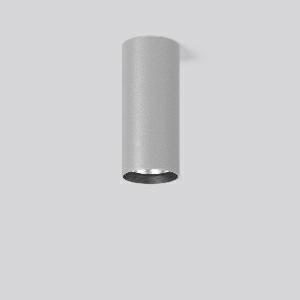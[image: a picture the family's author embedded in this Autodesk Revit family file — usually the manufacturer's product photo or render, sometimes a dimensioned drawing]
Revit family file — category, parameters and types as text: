
# Revit family: heledon_mini_a_931202_004_1_76_789c
name_source: partatom
category: Lighting Fixtures
units: mm (PartAtom-declared; Revit-internal decimal feet)

## family parameters
Cut with Voids When Loaded = No
Host = Face
Light Source = No
Part Type = Normal
Room Calculation Point = No
Round Connector Dimension = Use Diameter
Shared = No

## types (1)
- HELEDON mini A (1 x LED Modul 940, 2750 lm, 4000)
    Apparent Load = 20 VA
    Approval mark = CE
    CIE Flux Codes = 95 99 100 100 100
    Color Rendering = 92
    Color Temperature = 4000
    Default Elevation = 1800 mm
    Description = Series: HELEDON mini
Cylindrical surface-mounted downlight. Housing: die-cast aluminium, powder-coated. Internal ceiling frame polycarbonate with bayonet mounting. Black plastic ring and recessed LED to prevent glare from the side. Optical assembly with reflector made of MIRO-Silver with 98% total light reflection for outstanding efficiency - can be changed without tools. Best colour rendering index Ra>90. Suitable for Ceiling mounting. Easy installation with a separate ceiling frame with bayonet mounting and plug connection. Driver integrated. Connected via plug-in connector. High quality converter without flickering and stroboscopic effect. The following accessories can be mounted without use of tools: interchangeable lenses, decorative glasses, honeycomb louvre, clear and frosted diffusers, white interchangeable plastic ring. 
Colour: silver
Diameter: 87 mm
Height: 197 mm
Lamp: LED
Socket: without socket
Colour temperature: 4000K
Colour rendering index (CRI): 92
System power: 20 W
Rated luminous flux: 2750 lm
Luminous efficiency: 138 lm/W
Control gear: Converter, dimmable, DALI
Protection class: I
Type of protection: IP 20
    Height = 197 mm
    Lamp = 1 x LED Modul 940
    Lamp Light Flux = 2750 lm
    Lamp count = 1
    Length = 87 mm
    Lifetime = 50000 h
    Luminous efficacy = 138 lm/W
    Manufacturer = RZB
    ModVariant = No
    Model = 931202.004.1.76
    Mounting Place = Ceiling
    Mounting Type = Surface mounted
    Number of Poles = 1
    OnlyDefault = Yes
    Power Factor = 1
    Product Name = HELEDON mini A
    Product group = Surface mounted downlights
    ProductGroupID = 302
    Protection Class = Protection class I
    Protection Degree = IP 20
    RLX_Detail_Level = 1
    RLX_Emergency_Light_Flux = 0 lm
    RLX_Emergency_Type = 0
    RLX_Emergency_Type_DB = No
    RlxData = <blob elided: 107537 chars, md5=f5f3c9b7>
    Socket = socket
    Standby Power = 0 W
    System Light Flux = 2750 lm
    System Power = 20 W
    Type Comments = Product without accessories
    Type Image = 931188.004.jpg
    URL = http://relux.com
    VarID = ---
    Voltage = 230 V
    Voltage Range = 220-240 V
    Weight = 0.00 kg
    Width = 0 mm  [stored 0 ft]

note: [stored X ft] marks values corroborated as IEEE doubles in the binary element streams (Revit-internal decimal feet)

## geometry (parser evidence)
native form markers: Blend x4, Sweep x10
no freeform markers — native parametric forms only
